# Revit family: STOCK ADVANTAGE
name_source: partatom
category: Осветительные приборы
revit_build: Autodesk Revit 2016 (Build: 20150220_1215(x64)
units: mm (PartAtom-declared; Revit-internal decimal feet)

## family parameters
Источник света = Да
Общий = Нет
Основа = Грань
При загрузке вырезать с полостями = Нет
Размер круглого соединителя = Использовать диаметр
Тип детали = Нормальный
Точка расчета площади = Нет

## types (1)
- STOCK ADVANTAGE
    ADSK_Единица измерения = Шт.
    ADSK_Завод-изготовитель = ООО МГК Световые технологии
    ADSK_Код изделия = 1347001440
    ADSK_Количество фаз = 1
    ADSK_Количество фаз числовое = 1
    ADSK_Коэффициент мощности = 0.96
    ADSK_Масса = 7.6
    ADSK_Наименование = Серия энергоэффективных светильников для освещения промышленных цехов и логистических комплексов с потолками выше 12 метров. Для тяжелых условий эксплуатации предусмотрены модификации с прозрачным темперированным стеклом со степенью защиты IP65. В светильнике применяются люминесцентные лампы Т5
    ADSK_Напряжение = 230 В
    ADSK_Номинальная мощность = 0 кВт
    ADSK_Полная мощность = 0 кВ·А
    ADSK_Размер_Высота = 114 мм
    ADSK_Размер_Длина = 1293 мм
    ADSK_Размер_Ширина = 301 мм
    ADSK_Ток = 0 А
    ADSK_Энергоэффективность = 113 лм/Вт
    IP Class = IP54
    URL = https://www.ltcompany.com
    Блок аварийного питания = Нет
    Видимая форма излучения при визуализации = Нет
    Группа модели = Светильники
    Изготовитель = ООО МГК Световые технологии
    Излучение по длине прямоугольника = 1293 мм
    Излучение по ширине прямоугольника = 301 мм
    Класс Защиты = I
    Класс пожароопасности = П-I,II,IIa,ІІІ
    Климатическая зона = УХЛ2
    Код по классификатору = D5020200
    Корпус = Черный металл
    Корпус.высота = 85 мм
    Крепление.высота = 29 мм
    Крепление.ширина = 156 мм
    Крышка.рама = Cерый металл
    Крышка.стекло = Плафон полупрозрачный
    Лампы = Плафон самосвечение
    Область использования = Гипер- /супермаркеты, Промышленные предприятия, Складские объекты, ТРЦ
    Описание = Серия энергоэффективных светильников для освещения промышленных цехов и логистических комплексов с потолками выше 12 метров. Для тяжелых условий эксплуатации предусмотрены модификации с прозрачным темперированным стеклом со степенью защиты IP65. В светильнике применяются люминесцентные лампы Т5
    Отметка по умолчанию = 0 мм
    Отражатель = Корпус металл
    Подвес.материал = Cерый металл
    Подвес.ширина = 810 мм
    Полная установленная мощность = 0 кВ·А
    Разработчик = ООО ПРОРУБИМ
    Разработчик (телефон) = +7 (495) 649-85-43
    Светофильтр = 16777215
    Смещение цветовой температуры при затухании лампы = <Нет>
    Тип ИС = ЛЛ
    Тип ПРА = ЭПРА
    Тип продукции = Светильник
    Угол наклона = -90.00°
    Файл фотометрической сетки = generic
